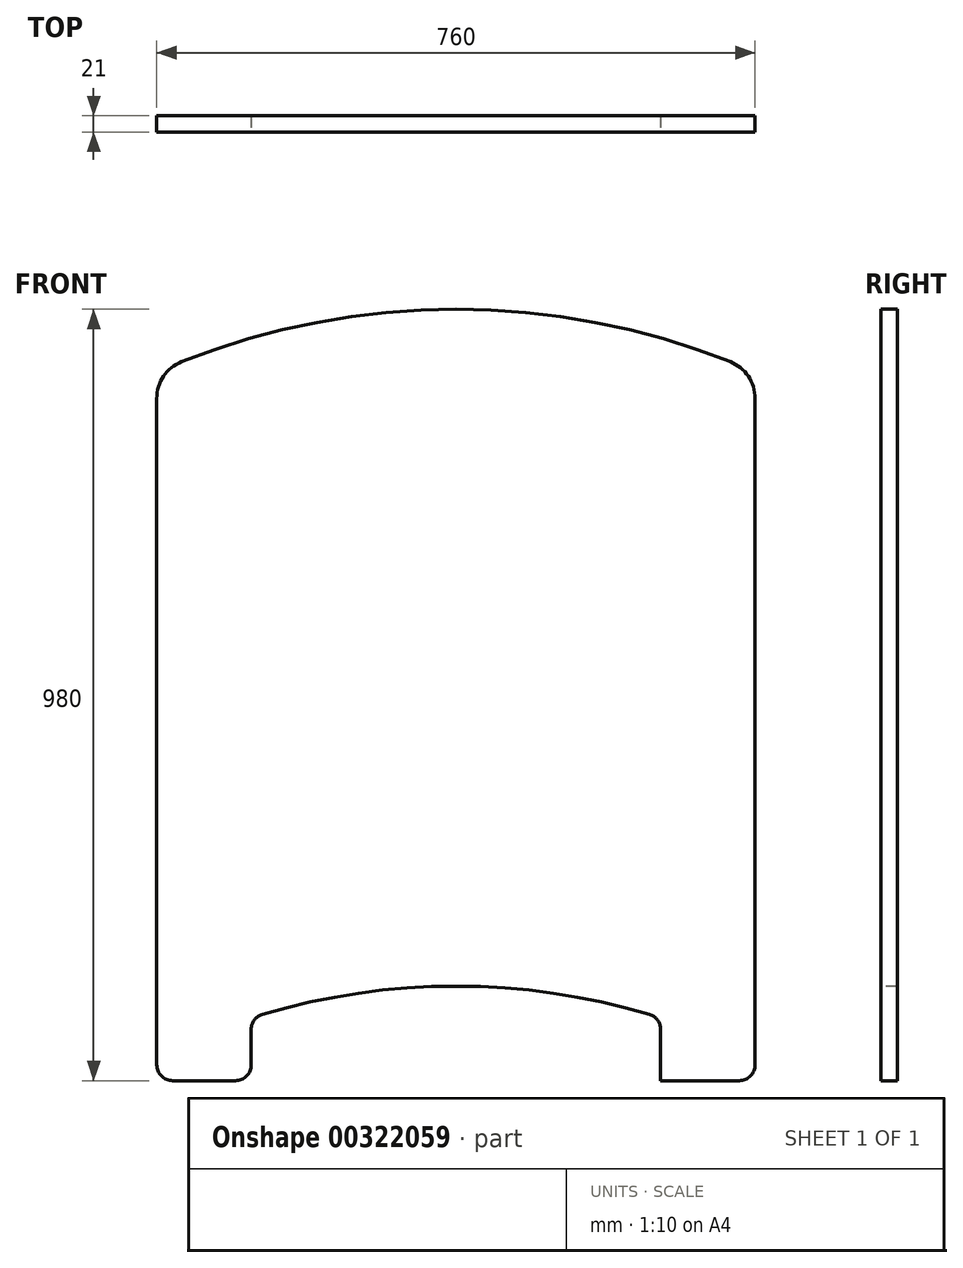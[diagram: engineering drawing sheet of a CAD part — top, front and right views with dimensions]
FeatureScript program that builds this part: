
annotation { "Feature Type Name" : "Feature", "Feature Type Description" : "" }
export const myFeature = defineFeature(function(context is Context, id is Id, definition is map)
    precondition{}
    {
        {
            var Q0;
            Q0=qCreatedBy(makeId("Front.planeOp"),FACE);
            var sketch = newSketch(context, id + "F0", { "sketchPlane" : qUnion([Q0])});
            skLineSegment(sketch, "E0.top", {"start": v(380, -490) * mm, "end": v(-380, -490) * mm});
            skLineSegment(sketch, "E0.left", {"start": v(380, 410) * mm, "end": v(380, -490) * mm});
            skLineSegment(sketch, "E0.right", {"start": v(-380, 410) * mm, "end": v(-380, -490) * mm});
            skPoint(sketch, "E0.middle", {"position": v(0, 0) * mm});
            skArc(sketch, "E1", {"start": v(380, 410) * mm, "mid": v(0, 490) * mm, "end": v(-380, 410) * mm});
            skPoint(sketch, "E2.orphan", {"position": v(380, 490) * mm});
            skLineSegment(sketch, "E3", {"start": v(-380, 410) * mm, "end": v(-380, 490) * mm, "construction": true});
            skLineSegment(sketch, "E4", {"start": v(380, 490) * mm, "end": v(380, 410) * mm, "construction": true});
            skLineSegment(sketch, "E5", {"start": v(-380, 490) * mm, "end": v(380, 490) * mm, "construction": true});
            skSolve(sketch);
        }
        {
            var Q0;
            Q0=makeQuery(id+"F0.imprint","IMPRINT",FACE,{"disambiguationData":[TD([[makeQuery(id+"F0.imprint","IMPRINT",EDGE,{"derivedFrom":sQuery(id+"F0.wireOp",EDGE,"E0.top")}),-1.0]])]});
            extrude(context, id + "F1", {"entities" : qUnion([Q0]), "endBound" : BoundingType.SYMMETRIC, "depth" : .1 * mm});
        }
        {
            var Q0;
            Q0=makeQuery(id+"F1.opExtrude","CAP_FACE",FACE,{"disambiguationData":[OSD([sQuery(id+"F0.wireOp",EDGE,"E0.top"),sQuery(id+"F0.wireOp",EDGE,"E0.left"),sQuery(id+"F0.wireOp",EDGE,"E0.right"),sQuery(id+"F0.wireOp",EDGE,"E1")])],"isStart":false});
            var sketch = newSketch(context, id + "F2", { "sketchPlane" : qUnion([Q0])});
            skLineSegment(sketch, "E6", {"start": v(-260, -490) * mm, "end": v(-260, -410) * mm});
            skLineSegment(sketch, "E7", {"start": v(260, -490) * mm, "end": v(260, -410) * mm});
            skArc(sketch, "E8", {"start": v(260, -410) * mm, "mid": v(0, -370) * mm, "end": v(-260, -410) * mm});
            skPoint(sketch, "E9", {"position": v(0, -370) * mm});
            skLineSegment(sketch, "E10", {"start": v(-260, -490) * mm, "end": v(260, -490) * mm});
            skSolve(sketch);
        }
        {
            var Q0;
            Q0 = qSketchRegion(id + "F2", true);
            extrude(context, id + "F3", {"entities" : qUnion([Q0]), "operationType" : NewBodyOperationType.REMOVE, "endBound" : BoundingType.UP_TO_NEXT, "oppositeDirection" : true, "depth" : 25 * mm});
        }
        {
            var Q0;
            Q0=makeQuery(id+"F1.opExtrude","SWEPT_EDGE",EDGE,{"disambiguationData":[OSD([sQuery(id+"F0.wireOp",EDGE,"E0.top"),sQuery(id+"F0.wireOp",EDGE,"E0.right")])]});
            var Q1;
            Q1=makeQuery(id+"F3.boolean.opBoolean","COPY",EDGE,{"derivedFrom":makeQuery(id+"F3.opExtrude","SWEPT_EDGE",EDGE,{"disambiguationData":[OSD([sQuery(id+"F0.wireOp",EDGE,"E0.top"),sQuery(id+"F2.wireOp",EDGE,"E6"),sQuery(id+"F2.wireOp",EDGE,"E10")])]})});
            var Q2;
            Q2=makeQuery(id+"F1.opExtrude","SWEPT_EDGE",EDGE,{"disambiguationData":[OSD([sQuery(id+"F0.wireOp",EDGE,"E0.top"),sQuery(id+"F0.wireOp",EDGE,"E0.left")])]});
            var Q3;
            Q3=makeQuery(id+"F3.boolean.opBoolean","COPY",EDGE,{"derivedFrom":makeQuery(id+"F3.opExtrude","SWEPT_EDGE",EDGE,{"disambiguationData":[OSD([sQuery(id+"F0.wireOp",EDGE,"E0.top"),sQuery(id+"F2.wireOp",EDGE,"E7"),sQuery(id+"F2.wireOp",EDGE,"E10")])]})});
            fillet(context, id + "F4", {"entities" : qUnion([Q0, Q1, Q2, Q3]), "radius" : 20 * mm, "tangentPropagation" : true, "allowEdgeOverflow" : false});
        }
        {
            var Q0;
            Q0=makeQuery(id+"F1.opExtrude","SWEPT_EDGE",EDGE,{"disambiguationData":[OSD([sQuery(id+"F0.wireOp",EDGE,"E0.right"),sQuery(id+"F0.wireOp",EDGE,"E1")])]});
            var Q1;
            Q1=makeQuery(id+"F1.opExtrude","SWEPT_EDGE",EDGE,{"disambiguationData":[OSD([sQuery(id+"F0.wireOp",EDGE,"E0.left"),sQuery(id+"F0.wireOp",EDGE,"E1")])]});
            fillet(context, id + "F5", {"entities" : qUnion([Q0, Q1]), "radius" : 50 * mm, "tangentPropagation" : true, "allowEdgeOverflow" : false});
        }
        {
            var Q0;
            Q0=makeQuery(id+"F3.boolean.opBoolean","COPY",EDGE,{"derivedFrom":makeQuery(id+"F3.opExtrude","SWEPT_EDGE",EDGE,{"disambiguationData":[OSD([sQuery(id+"F2.wireOp",EDGE,"E6"),sQuery(id+"F2.wireOp",EDGE,"E8")])]})});
            var Q1;
            Q1=makeQuery(id+"F3.boolean.opBoolean","COPY",EDGE,{"derivedFrom":makeQuery(id+"F3.opExtrude","SWEPT_EDGE",EDGE,{"disambiguationData":[OSD([sQuery(id+"F2.wireOp",EDGE,"E7"),sQuery(id+"F2.wireOp",EDGE,"E8")])]})});
            fillet(context, id + "F6", {"entities" : qUnion([Q0, Q1]), "radius" : 20 * mm, "tangentPropagation" : true, "allowEdgeOverflow" : false});
        }
        {
            var Q0;
            Q0=makeQuery(id+"F1.opExtrude","CAP_FACE",FACE,{"disambiguationData":[OSD([sQuery(id+"F0.wireOp",EDGE,"E0.top"),sQuery(id+"F0.wireOp",EDGE,"E0.left"),sQuery(id+"F0.wireOp",EDGE,"E0.right"),sQuery(id+"F0.wireOp",EDGE,"E1")])],"isStart":true});
            extrude(context, id + "F7", {"entities" : qUnion([Q0]), "depth" : 20.8 * mm});
        }
        {
            var Q0;
            Q0=makeQuery(id+"F7.opExtrude","CAP_FACE",FACE,{"disambiguationData":[OSD([sQuery(id+"F0.wireOp",EDGE,"E0.top"),sQuery(id+"F0.wireOp",EDGE,"E0.left"),sQuery(id+"F0.wireOp",EDGE,"E0.right"),sQuery(id+"F0.wireOp",EDGE,"E1")])],"isStart":false});
            extrude(context, id + "F8", {"entities" : qUnion([Q0]), "depth" : .1 * mm});
        }
    });
